# Revit family: P191568KX-125c_KCGC558J
name_source: partatom
category: Specialty Equipment
units: mm (PartAtom-declared; Revit-internal decimal feet)

## family parameters
Always vertical = Yes
Cut with Voids When Loaded = No
Enable Cutting in Views = No
Maintain Annotation Orientation = No
Part Type = Normal
Room Calculation Point = No
Round Connector Dimension = Use Diameter
Shared = No
Work Plane-Based = No

## types (1)
- KCGC558JSS
    Amps = 0 A
    Body Material = ARCAT - Metal - Steel - Stainless
    Cooking Grate Material = ARCAT - Metal - Cast Iron 1/4" Plate
    Default Elevation = 0"
    Depth = 27 7/8"
    Description = KitchenAid® 48'' 6-Burner Commercial-Style Gas Rangetop with Griddle
KitchenAid® 48'' 6-Burner Commercial-Style Gas Rangetop with Griddle
    Dimension Guide = https://www.whirlpool.com
https://www.whirlpool.com
    Family Name = COOKING
    Feature 1 = Two 20,000 BTU Ultra Power™ Dual-Flame Burners
Two 20,000 BTU Ultra Power™ Dual-Flame Burners
    Feature 2 = 5,000 BTU Simmer & Melt Burner
5,000 BTU Simmer & Melt Burner
    Feature 3 = Three-Level Convertible Grates
Three-Level Convertible Grates
    Height = 7 7/16"
    Installation-Fabrication = https://www.whirlpool.com
https://www.whirlpool.com
    Knob Material = ARCAT - Metal - Steel - Gray
    Manufacturer = KitchenAid
    Model = KCGC558JSS
    Voltage = 0 V
    Width = 47 7/8"

## geometry (parser evidence)
native form markers: Sweep x5
no freeform markers — native parametric forms only
